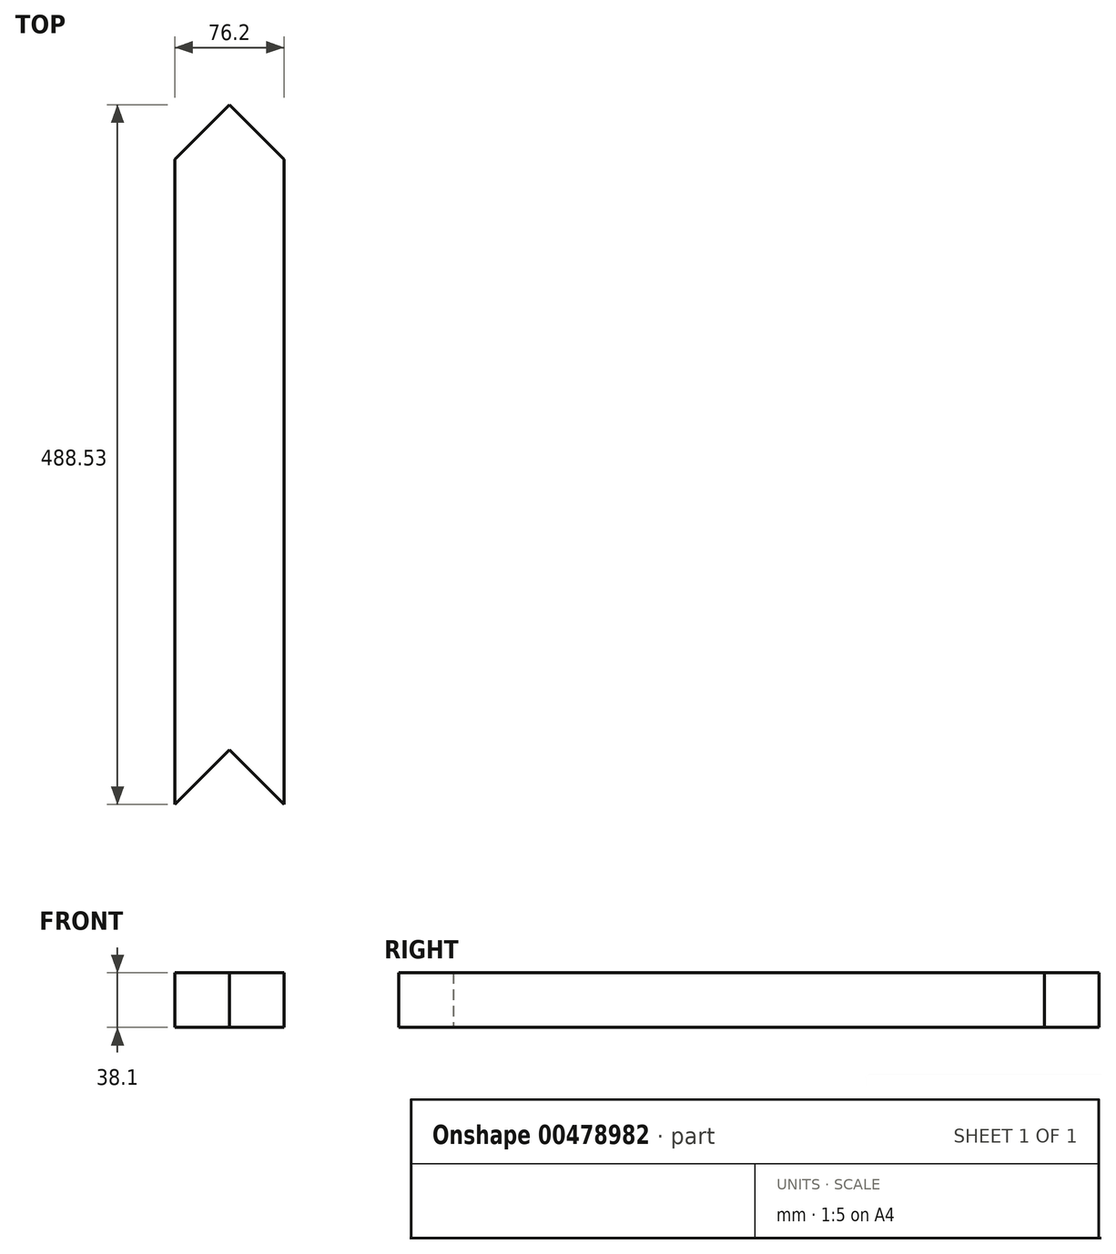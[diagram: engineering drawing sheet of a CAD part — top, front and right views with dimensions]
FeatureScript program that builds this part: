
annotation { "Feature Type Name" : "Feature", "Feature Type Description" : "" }
export const myFeature = defineFeature(function(context is Context, id is Id, definition is map)
    precondition{}
    {
        {
            var Q0;
            Q0=qCreatedBy(makeId("Top.planeOp"),FACE);
            var sketch = newSketch(context, id + "F0", { "sketchPlane" : qUnion([Q0])});
            skLineSegment(sketch, "E0", {"start": v(0, 0) * mm, "end": v(38.1, -38.1) * mm});
            skLineSegment(sketch, "E1", {"start": v(38.1, -38.1) * mm, "end": v(38.1, 412.33) * mm});
            skLineSegment(sketch, "E2", {"start": v(38.1, 412.33) * mm, "end": v(0, 450.43) * mm});
            skLineSegment(sketch, "E3", {"start": v(0, 450.43) * mm, "end": v(-38.1, 412.33) * mm});
            skLineSegment(sketch, "E4", {"start": v(-38.1, 412.33) * mm, "end": v(-38.1, -38.1) * mm});
            skLineSegment(sketch, "E5", {"start": v(-38.1, -38.1) * mm, "end": v(0, 0) * mm});
            skSolve(sketch);
        }
        {
            var Q0;
            Q0=makeQuery(id+"F0.imprint","IMPRINT",FACE,{"disambiguationData":[TD([[makeQuery(id+"F0.imprint","IMPRINT",EDGE,{"derivedFrom":sQuery(id+"F0.wireOp",EDGE,"E0")}),1.0]])]});
            extrude(context, id + "F1", {"entities" : qUnion([Q0]), "depth" : 38.1 * mm});
        }
    });
